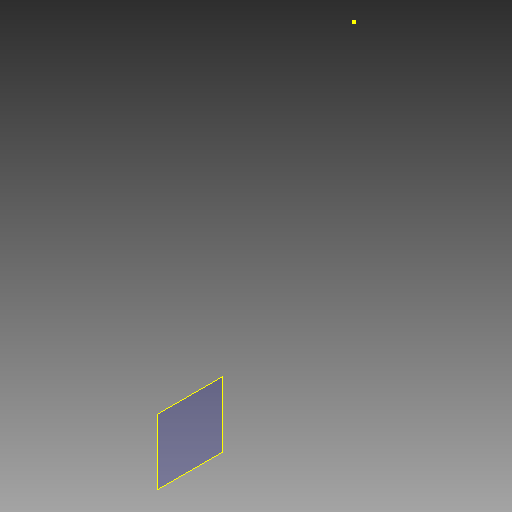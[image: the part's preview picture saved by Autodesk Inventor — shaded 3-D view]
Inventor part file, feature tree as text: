
AUTODESK INVENTOR PART (.ipt)
format: ipt  version: 2019 (Build 230136000, 136)  size: 110,592 bytes
history: native  units: in
note: dims shown in document units (in); Inventor stores cm internally (conversion verified against a paired STEP export)
features: sketch x5, hole x2, plane x1, extrude x1
ambient origin geometry x8: Origin, YZ Plane, XZ Plane, XY Plane, X Axis, Y Axis, Z Axis, Center Point
feature tree (9):
  plane  "Work Plane1"
  extrude  "Extrusion3"  [1 undecoded]
  hole  "Hole2"  [1 undecoded]
  hole  "Hole3"  [1 undecoded]
  sketch  "Sketch12"
  sketch  "Sketch13"
  sketch  "Sketch8"  dims[d25=1.6in d26=0.0in]
  sketch  "Sketch10"  dims[d28=0.196in d29=0.5in d30=0.375in d31=0.25in d32=0.5635in d33=1.0in d34=0.8108in]
  sketch  "Sketch11"  dims[d35=0.196in d36=0.5in d37=0.375in d38=0.25in d39=0.5635in d40=1.0in d41=0.8108in]
note: 3 required parameter values undecoded (feature->parameter linkage not recoverable at this tier; creation-order binding heuristic only, values carry confidence <= 0.55)
